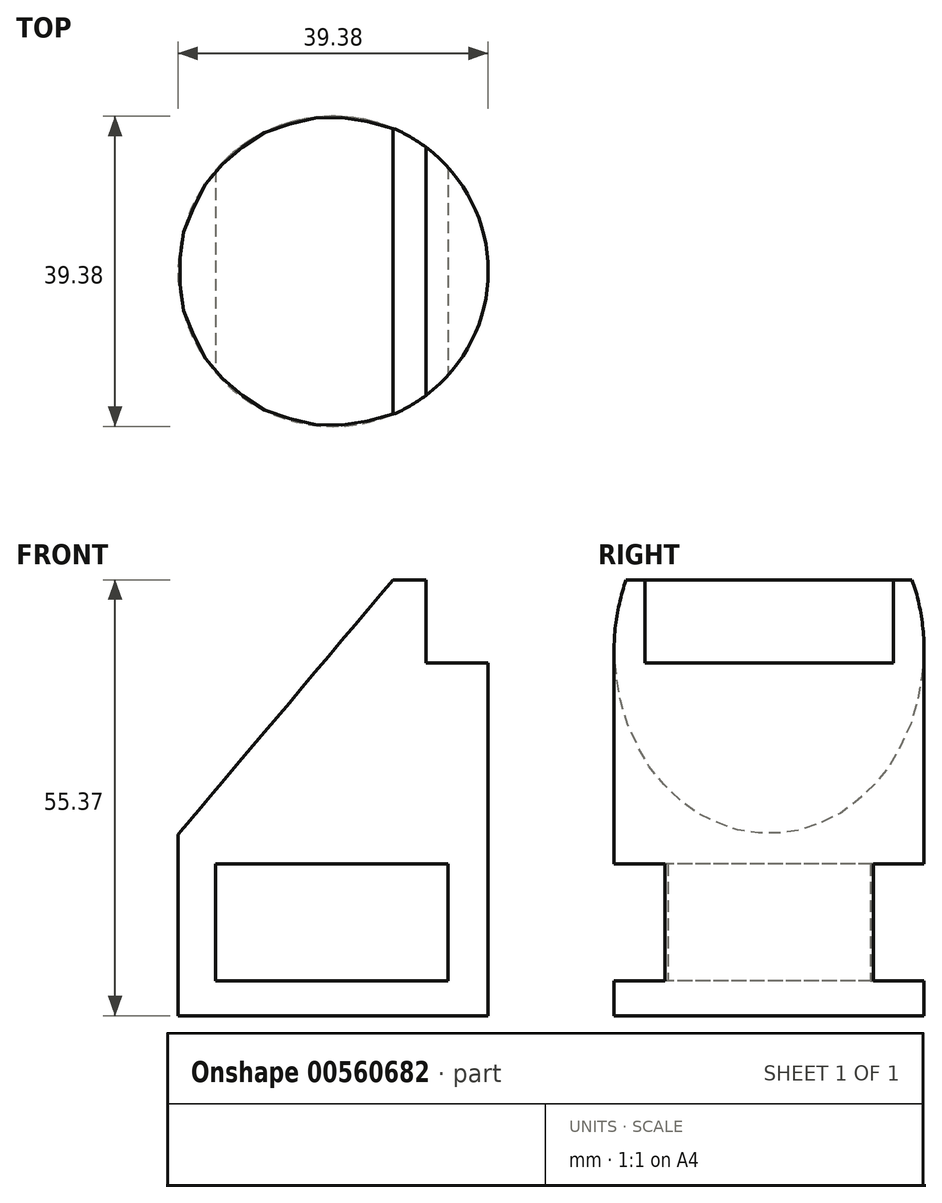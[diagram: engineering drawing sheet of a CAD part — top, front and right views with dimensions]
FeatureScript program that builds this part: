
annotation { "Feature Type Name" : "Feature", "Feature Type Description" : "" }
export const myFeature = defineFeature(function(context is Context, id is Id, definition is map)
    precondition{}
    {
        {
            var Q0;
            Q0=qCreatedBy(makeId("Top.planeOp"),FACE);
            var sketch = newSketch(context, id + "F0", { "sketchPlane" : qUnion([Q0])});
            skCircle(sketch, "E0", {"center": v(0, 0) * mm, "radius": 19.7 * mm});
            skSolve(sketch);
        }
        {
            var Q0;
            Q0 = qSketchRegion(id + "F0", true);
            extrude(context, id + "F1", {"entities" : qUnion([Q0]), "depth" : 55.37 * mm, "offsetDistance" : 25.4 * mm});
        }
        {
            var Q0;
            Q0=qCreatedBy(makeId("Front.planeOp"),FACE);
            cPlane(context, id + "F2", {"entities" : qUnion([Q0]), "cplaneType" : CPlaneType.OFFSET, "offset" : 62.74 * mm, "width" : 152.4 * mm, "height" : 152.4 * mm});
        }
        {
            var Q0;
            Q0=qCreatedBy(id+"F2.planeOp",FACE);
            var sketch = newSketch(context, id + "F3", { "sketchPlane" : qUnion([Q0])});
            skLineSegment(sketch, "E1", {"start": v(11.8, 56.21) * mm, "end": v(11.8, 44.83) * mm});
            skLineSegment(sketch, "E2", {"start": v(11.8, 44.83) * mm, "end": v(23.88, 44.83) * mm});
            skLineSegment(sketch, "E3", {"start": v(23.88, 44.83) * mm, "end": v(23.88, 61.8) * mm});
            skLineSegment(sketch, "E4", {"start": v(23.88, 61.8) * mm, "end": v(11.8, 56.21) * mm});
            skSolve(sketch);
        }
        {
            var Q0;
            Q0=makeQuery(id+"F3.imprint","IMPRINT",FACE,{"disambiguationData":[TD([[makeQuery(id+"F3.imprint","IMPRINT",EDGE,{"derivedFrom":sQuery(id+"F3.wireOp",EDGE,"E1")}),1.0]])]});
            extrude(context, id + "F4", {"entities" : qUnion([Q0]), "operationType" : NewBodyOperationType.REMOVE, "oppositeDirection" : true, "depth" : 114.05 * mm, "offsetDistance" : 25.4 * mm});
        }
        {
            var Q0;
            Q0=qCreatedBy(id+"F2.planeOp",FACE);
            var sketch = newSketch(context, id + "F5", { "sketchPlane" : qUnion([Q0])});
            skLineSegment(sketch, "E5", {"start": v(0, 56.45) * mm, "end": v(8.54, 56.45) * mm});
            skLineSegment(sketch, "E6", {"start": v(8.54, 56.45) * mm, "end": v(-21.9, 20.43) * mm});
            skLineSegment(sketch, "E7", {"start": v(-21.9, 20.43) * mm, "end": v(-21.9, 57.6) * mm});
            skLineSegment(sketch, "E8", {"start": v(-21.9, 57.6) * mm, "end": v(0, 56.45) * mm});
            skLineSegment(sketch, "E9", {"start": v(-14.93, 14.38) * mm, "end": v(-14.93, 4.4) * mm});
            skLineSegment(sketch, "E10", {"start": v(-14.93, 4.4) * mm, "end": v(14.58, 4.4) * mm});
            skLineSegment(sketch, "E11", {"start": v(14.58, 4.4) * mm, "end": v(14.58, 19.26) * mm});
            skLineSegment(sketch, "E12", {"start": v(14.58, 19.26) * mm, "end": v(-14.93, 19.26) * mm});
            skLineSegment(sketch, "E13", {"start": v(-14.93, 19.26) * mm, "end": v(-14.93, 14.38) * mm});
            skSolve(sketch);
        }
        {
            var Q0;
            Q0=makeQuery(id+"F5.imprint","IMPRINT",FACE,{"disambiguationData":[TD([[makeQuery(id+"F5.imprint","IMPRINT",EDGE,{"derivedFrom":sQuery(id+"F5.wireOp",EDGE,"E9")}),1.0]])]});
            var Q1;
            Q1=makeQuery(id+"F5.imprint","IMPRINT",FACE,{"disambiguationData":[TD([[makeQuery(id+"F5.imprint","IMPRINT",EDGE,{"derivedFrom":sQuery(id+"F5.wireOp",EDGE,"E5")}),-1.0]])]});
            extrude(context, id + "F6", {"entities" : qUnion([Q0, Q1]), "operationType" : NewBodyOperationType.REMOVE, "oppositeDirection" : true, "depth" : 254 * mm, "offsetDistance" : 25.4 * mm});
        }
    });
